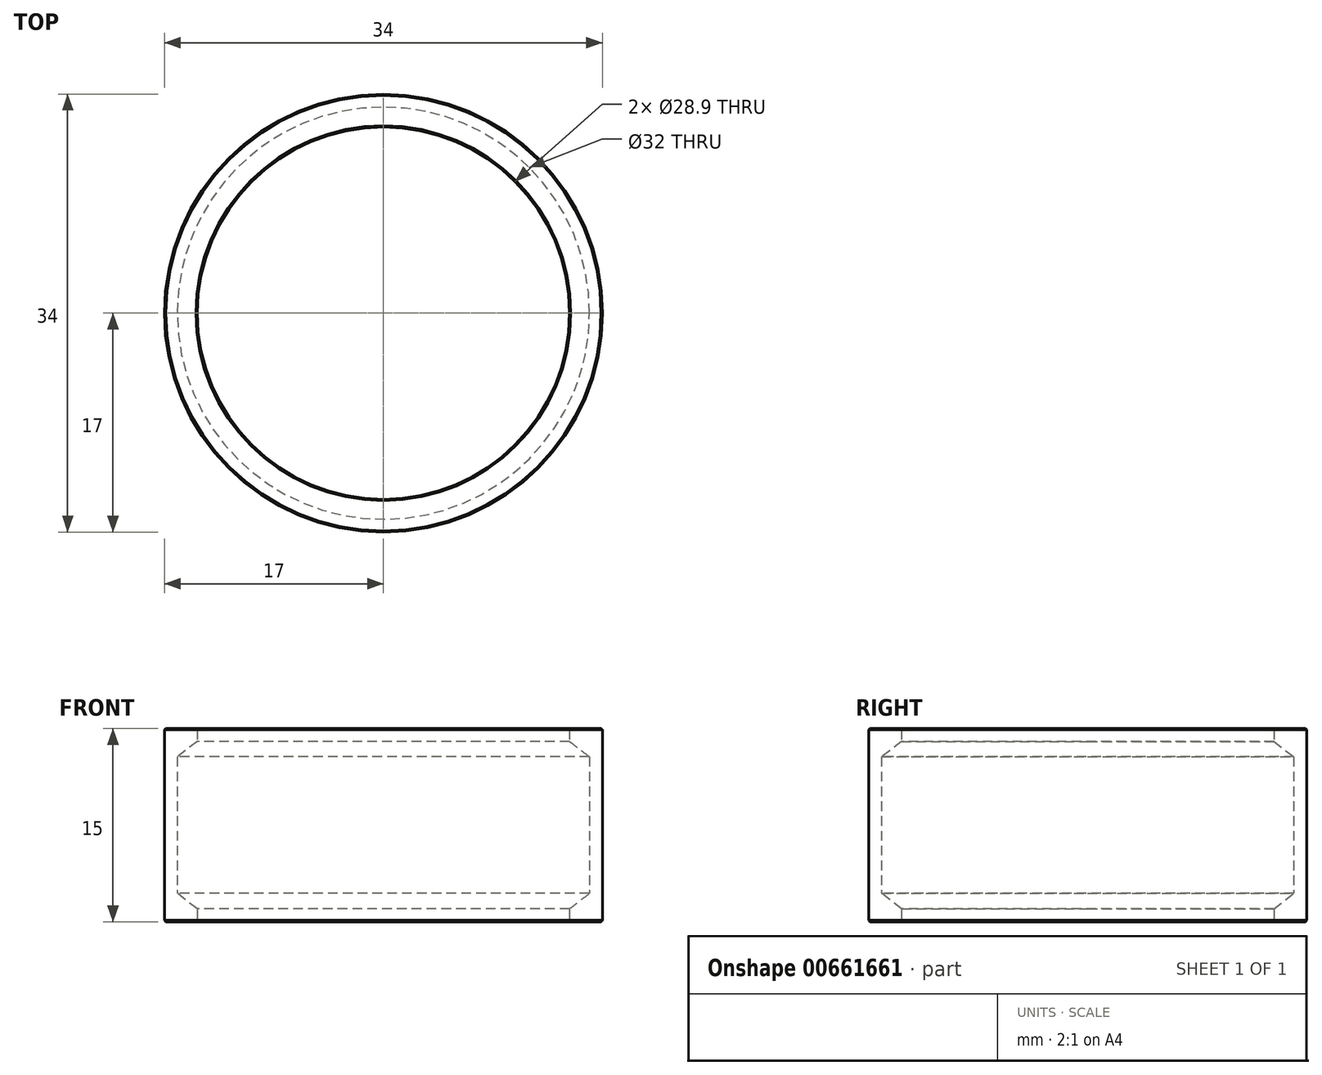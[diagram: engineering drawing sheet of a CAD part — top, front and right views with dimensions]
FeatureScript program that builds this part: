
annotation { "Feature Type Name" : "Feature", "Feature Type Description" : "" }
export const myFeature = defineFeature(function(context is Context, id is Id, definition is map)
    precondition{}
    {
        {
            var Q0;
            Q0=qCreatedBy(makeId("Top.planeOp"),FACE);
            var sketch = newSketch(context, id + "F0", { "sketchPlane" : qUnion([Q0])});
            skCircle(sketch, "E0", {"center": v(0, 0) * mm, "radius": 14.45 * mm});
            skCircle(sketch, "E1", {"center": v(0, 0) * mm, "radius": 17 * mm});
            skCircle(sketch, "E2", {"center": v(0, 0) * mm, "radius": 16 * mm});
            skSolve(sketch);
        }
        {
            var Q0;
            Q0=makeQuery(id+"F0.imprint","IMPRINT",FACE,{"disambiguationData":[TD([[makeQuery(id+"F0.imprint","IMPRINT",EDGE,{"derivedFrom":sQuery(id+"F0.wireOp",EDGE,"E0")}),-1.0]])]});
            var Q1;
            Q1=makeQuery(id+"F0.imprint","IMPRINT",FACE,{"disambiguationData":[TD([[makeQuery(id+"F0.imprint","IMPRINT",EDGE,{"derivedFrom":sQuery(id+"F0.wireOp",EDGE,"E1")}),1.0]])]});
            extrude(context, id + "F1", {"entities" : qUnion([Q0, Q1]), "endBound" : BoundingType.SYMMETRIC, "depth" : 15 * mm, "offsetDistance" : 25 * mm});
        }
        {
            var Q0;
            Q0=makeQuery(id+"F0.imprint","IMPRINT",FACE,{"disambiguationData":[TD([[makeQuery(id+"F0.imprint","IMPRINT",EDGE,{"derivedFrom":sQuery(id+"F0.wireOp",EDGE,"E0")}),-1.0]])]});
            var Q1;
            Q1=makeQuery(id+"F1.opExtrude","CAP_FACE",FACE,{"disambiguationData":[OSD([sQuery(id+"F0.wireOp",EDGE,"E0"),sQuery(id+"F0.wireOp",EDGE,"E1")])],"isStart":false});
            var Q2;
            Q2=makeQuery(id+"F1.opExtrude","CAP_FACE",FACE,{"disambiguationData":[OSD([sQuery(id+"F0.wireOp",EDGE,"E0"),sQuery(id+"F0.wireOp",EDGE,"E1")])],"isStart":true});
            extrude(context, id + "F2", {"entities" : qUnion([Q0]), "operationType" : NewBodyOperationType.REMOVE, "endBound" : BoundingType.UP_TO_SURFACE, "depth" : 25 * mm, "endBoundEntityFace" : qUnion([Q1]), "hasOffset" : true, "offsetDistance" : 1 * mm, "hasSecondDirection" : true, "secondDirectionBound" : SecondDirectionBoundingType.UP_TO_SURFACE, "secondDirectionOppositeDirection" : true, "secondDirectionDepth" : 25 * mm, "secondDirectionBoundEntityFace" : qUnion([Q2]), "hasSecondDirectionOffset" : true, "secondDirectionOffsetDistance" : 1 * mm});
        }
        {
            var Q0;
            Q0=makeQuery(id+"F2.boolean.opBoolean","COPY",EDGE,{"derivedFrom":makeQuery(id+"F2.opExtrude","CAP_EDGE",EDGE,{"disambiguationData":[OSD([sQuery(id+"F0.wireOp",EDGE,"E2")])],"isStart":true})});
            var Q1;
            Q1=makeQuery(id+"F2.boolean.opBoolean","COPY",EDGE,{"derivedFrom":makeQuery(id+"F2.opExtrude","CAP_EDGE",EDGE,{"disambiguationData":[OSD([sQuery(id+"F0.wireOp",EDGE,"E2")])],"isStart":false})});
            chamfer(context, id + "F3", {"entities" : qUnion([Q0, Q1]), "chamferType" : ChamferType.TWO_OFFSETS, "width1" : 1.55 * mm, "oppositeDirection" : false, "width2" : 1.2 * mm, "tangentPropagation" : true});
        }
        {
            var Q0;
            Q0=makeQuery(id+"F1.opExtrude","CAP_EDGE",EDGE,{"disambiguationData":[OSD([sQuery(id+"F0.wireOp",EDGE,"E1")])],"isStart":false});
            var Q1;
            Q1=makeQuery(id+"F1.opExtrude","CAP_EDGE",EDGE,{"disambiguationData":[OSD([sQuery(id+"F0.wireOp",EDGE,"E1")])],"isStart":true});
            chamfer(context, id + "F4", {"entities" : qUnion([Q0, Q1]), "width" : 0.1 * mm, "tangentPropagation" : true});
        }
        {
            var Q0;
            Q0=makeQuery(id+"F1.opExtrude","CAP_EDGE",EDGE,{"disambiguationData":[OSD([sQuery(id+"F0.wireOp",EDGE,"E0")])],"isStart":false});
            var Q1;
            Q1=makeQuery(id+"F1.opExtrude","CAP_EDGE",EDGE,{"disambiguationData":[OSD([sQuery(id+"F0.wireOp",EDGE,"E0")])],"isStart":true});
            chamfer(context, id + "F5", {"entities" : qUnion([Q0, Q1]), "width" : 0.1 * mm, "tangentPropagation" : true});
        }
    });
